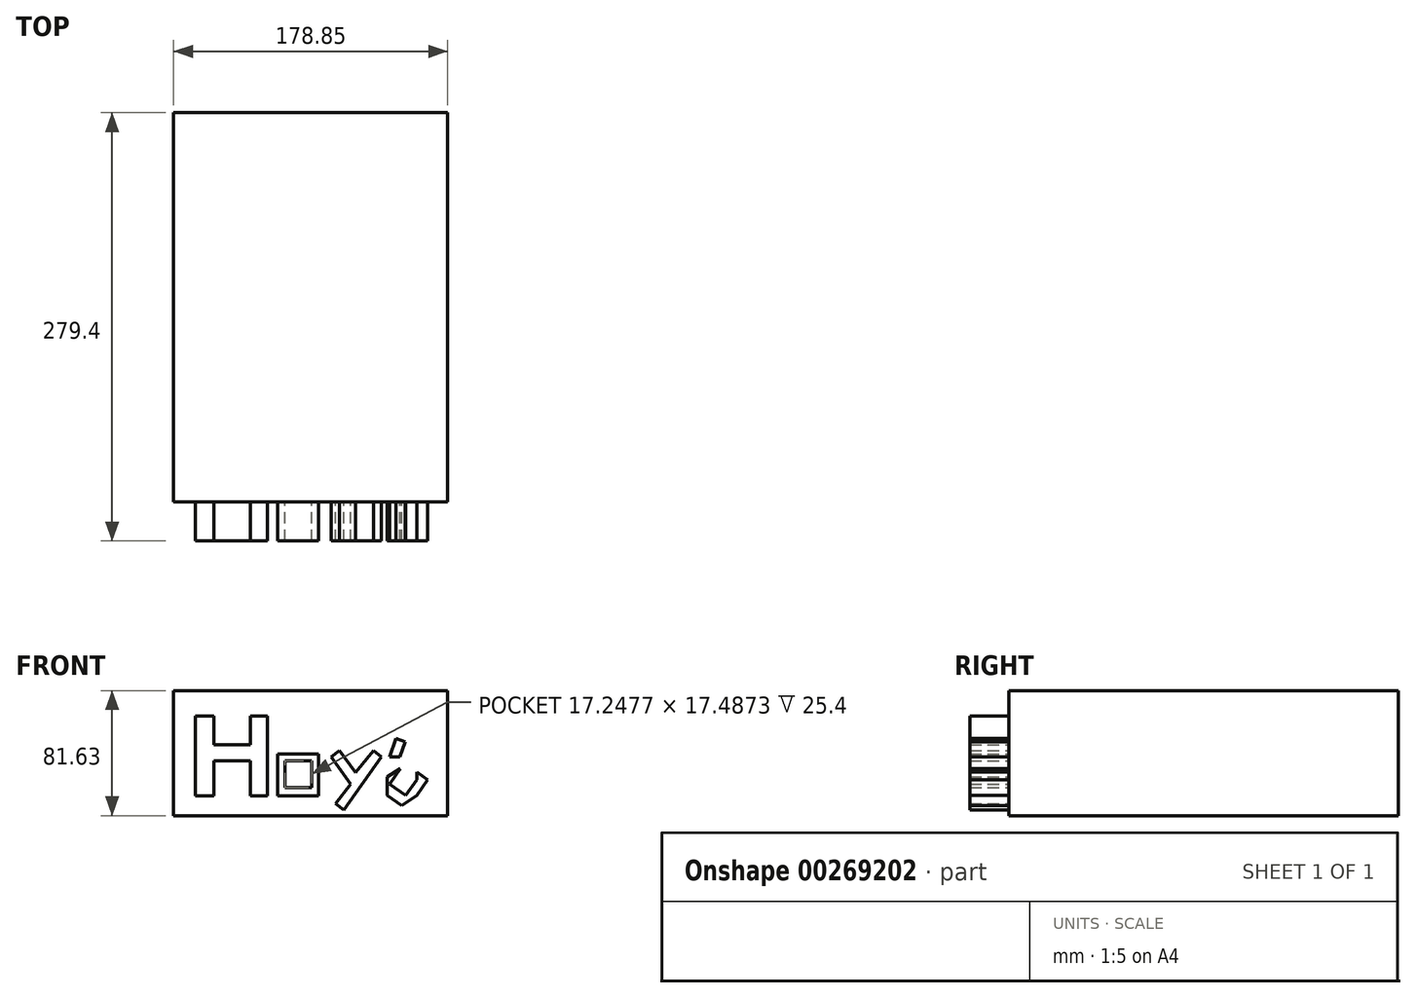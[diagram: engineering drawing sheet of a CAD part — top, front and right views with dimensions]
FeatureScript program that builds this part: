
annotation { "Feature Type Name" : "Feature", "Feature Type Description" : "" }
export const myFeature = defineFeature(function(context is Context, id is Id, definition is map)
    precondition{}
    {
        {
            var Q0;
            Q0=qCreatedBy(makeId("Front.planeOp"),FACE);
            var sketch = newSketch(context, id + "F0", { "sketchPlane" : qUnion([Q0])});
            skLineSegment(sketch, "E0.bottom", {"start": v(-50.1, 35.25) * mm, "end": v(128.76, 35.25) * mm});
            skLineSegment(sketch, "E0.top", {"start": v(-50.1, -46.38) * mm, "end": v(128.76, -46.38) * mm});
            skLineSegment(sketch, "E0.left", {"start": v(-50.1, 35.25) * mm, "end": v(-50.1, -46.38) * mm});
            skLineSegment(sketch, "E0.right", {"start": v(128.76, 35.25) * mm, "end": v(128.76, -46.38) * mm});
            skSolve(sketch);
        }
        {
            var Q0;
            Q0 = qSketchRegion(id + "F0", true);
            extrude(context, id + "F1", {"entities" : qUnion([Q0]), "depth" : 254 * mm});
        }
        {
            var Q0;
            Q0=qCreatedBy(makeId("Front.planeOp"),FACE);
            var sketch = newSketch(context, id + "F2", { "sketchPlane" : qUnion([Q0])});
            skLineSegment(sketch, "E1.bottom", {"start": v(-36, 18.68) * mm, "end": v(-23.78, 18.68) * mm});
            skLineSegment(sketch, "E1.top", {"start": v(-36, -33.54) * mm, "end": v(-23.78, -33.54) * mm});
            skLineSegment(sketch, "E1.left", {"start": v(-36, 18.68) * mm, "end": v(-36, -33.54) * mm});
            skLineSegment(sketch, "E1.right", {"start": v(-23.78, 18.68) * mm, "end": v(-23.78, -33.54) * mm});
            skLineSegment(sketch, "E2.bottom", {"start": v(-23.78, 0) * mm, "end": v(0, 0) * mm});
            skLineSegment(sketch, "E2.top", {"start": v(-23.78, -10.54) * mm, "end": v(0, -10.54) * mm});
            skLineSegment(sketch, "E2.left", {"start": v(-23.78, 0) * mm, "end": v(-23.78, -10.54) * mm});
            skLineSegment(sketch, "E2.right", {"start": v(0, 0) * mm, "end": v(0, -10.54) * mm});
            skLineSegment(sketch, "E3.bottom", {"start": v(0, 18.45) * mm, "end": v(11.19, 18.45) * mm});
            skLineSegment(sketch, "E3.top", {"start": v(0, -33.54) * mm, "end": v(11.19, -33.54) * mm});
            skLineSegment(sketch, "E3.left", {"start": v(0, 18.45) * mm, "end": v(0, -33.54) * mm});
            skLineSegment(sketch, "E3.right", {"start": v(11.19, 18.45) * mm, "end": v(11.19, -33.54) * mm});
            skLineSegment(sketch, "E4.bottom", {"start": v(17.9, -6.23) * mm, "end": v(44.49, -6.23) * mm});
            skLineSegment(sketch, "E4.top", {"start": v(17.9, -33.54) * mm, "end": v(44.49, -33.54) * mm});
            skLineSegment(sketch, "E4.left", {"start": v(17.9, -6.23) * mm, "end": v(17.9, -33.54) * mm});
            skLineSegment(sketch, "E4.right", {"start": v(44.49, -6.23) * mm, "end": v(44.49, -33.54) * mm});
            skLineSegment(sketch, "E5.bottom", {"start": v(22.69, -10.54) * mm, "end": v(39.94, -10.54) * mm});
            skLineSegment(sketch, "E5.top", {"start": v(22.69, -28.03) * mm, "end": v(39.94, -28.03) * mm});
            skLineSegment(sketch, "E5.left", {"start": v(22.69, -10.54) * mm, "end": v(22.69, -28.03) * mm});
            skLineSegment(sketch, "E5.right", {"start": v(39.94, -10.54) * mm, "end": v(39.94, -28.03) * mm});
            skLineSegment(sketch, "E6", {"start": v(52.63, -8.14) * mm, "end": v(65.57, -25.87) * mm});
            skLineSegment(sketch, "E7", {"start": v(52.63, -8.14) * mm, "end": v(58.25, -4.04) * mm});
            skLineSegment(sketch, "E8", {"start": v(58.25, -4.04) * mm, "end": v(68.71, -18.38) * mm});
            skLineSegment(sketch, "E9", {"start": v(68.71, -18.38) * mm, "end": v(80.18, -4.04) * mm});
            skLineSegment(sketch, "E10", {"start": v(80.18, -4.04) * mm, "end": v(85.3, -8.14) * mm});
            skLineSegment(sketch, "E11", {"start": v(85.3, -8.14) * mm, "end": v(61.02, -42.64) * mm});
            skLineSegment(sketch, "E12", {"start": v(61.02, -42.64) * mm, "end": v(55.43, -38.7) * mm});
            skLineSegment(sketch, "E13", {"start": v(55.43, -38.7) * mm, "end": v(65.57, -25.87) * mm});
            skLineSegment(sketch, "E14", {"start": v(94.8, 3.83) * mm, "end": v(90.72, -8.14) * mm});
            skLineSegment(sketch, "E15", {"start": v(94.8, 3.83) * mm, "end": v(100.88, 1.76) * mm});
            skLineSegment(sketch, "E16", {"start": v(100.88, 1.76) * mm, "end": v(97.51, -8.14) * mm});
            skLineSegment(sketch, "E17", {"start": v(97.51, -8.14) * mm, "end": v(90.72, -8.14) * mm});
            skLineSegment(sketch, "E18", {"start": v(115.56, 0) * mm, "end": v(108.46, -10.23) * mm});
            skLineSegment(sketch, "E19", {"start": v(115.56, 0) * mm, "end": v(122.93, -5.12) * mm});
            skPoint(sketch, "E19.endSnap0", {"position": v(112.01, -5.12) * mm});
            skLineSegment(sketch, "E20", {"start": v(122.4, -5.97) * mm, "end": v(115.56, -15.82) * mm});
            skLineSegment(sketch, "E21", {"start": v(108.46, -10.23) * mm, "end": v(108.46, -15.82) * mm});
            skLineSegment(sketch, "E22", {"start": v(108.46, -15.82) * mm, "end": v(115.56, -15.82) * mm});
            skLineSegment(sketch, "E23", {"start": v(89.24, -21.25) * mm, "end": v(89.24, -33.2) * mm});
            skLineSegment(sketch, "E24", {"start": v(89.24, -33.2) * mm, "end": v(98.64, -39.74) * mm});
            skLineSegment(sketch, "E25", {"start": v(98.64, -39.74) * mm, "end": v(108.46, -33.2) * mm});
            skLineSegment(sketch, "E26", {"start": v(108.46, -33.2) * mm, "end": v(115.56, -22.98) * mm});
            skLineSegment(sketch, "E27", {"start": v(115.56, -22.98) * mm, "end": v(108.46, -18.05) * mm});
            skLineSegment(sketch, "E28", {"start": v(108.46, -18.05) * mm, "end": v(108.46, -22.98) * mm});
            skLineSegment(sketch, "E29", {"start": v(108.46, -22.98) * mm, "end": v(101.36, -33.2) * mm});
            skLineSegment(sketch, "E30", {"start": v(101.36, -33.2) * mm, "end": v(90.8, -25.87) * mm});
            skLineSegment(sketch, "E31", {"start": v(90.8, -25.87) * mm, "end": v(97.77, -15.82) * mm});
            skLineSegment(sketch, "E32", {"start": v(97.77, -15.82) * mm, "end": v(89.24, -21.25) * mm});
            skSolve(sketch);
        }
        {
            var Q0;
            Q0 = qSketchRegion(id + "F2", true);
            extrude(context, id + "F3", {"entities" : qUnion([Q0]), "operationType" : NewBodyOperationType.ADD, "depth" : 279.4 * mm});
        }
    });
